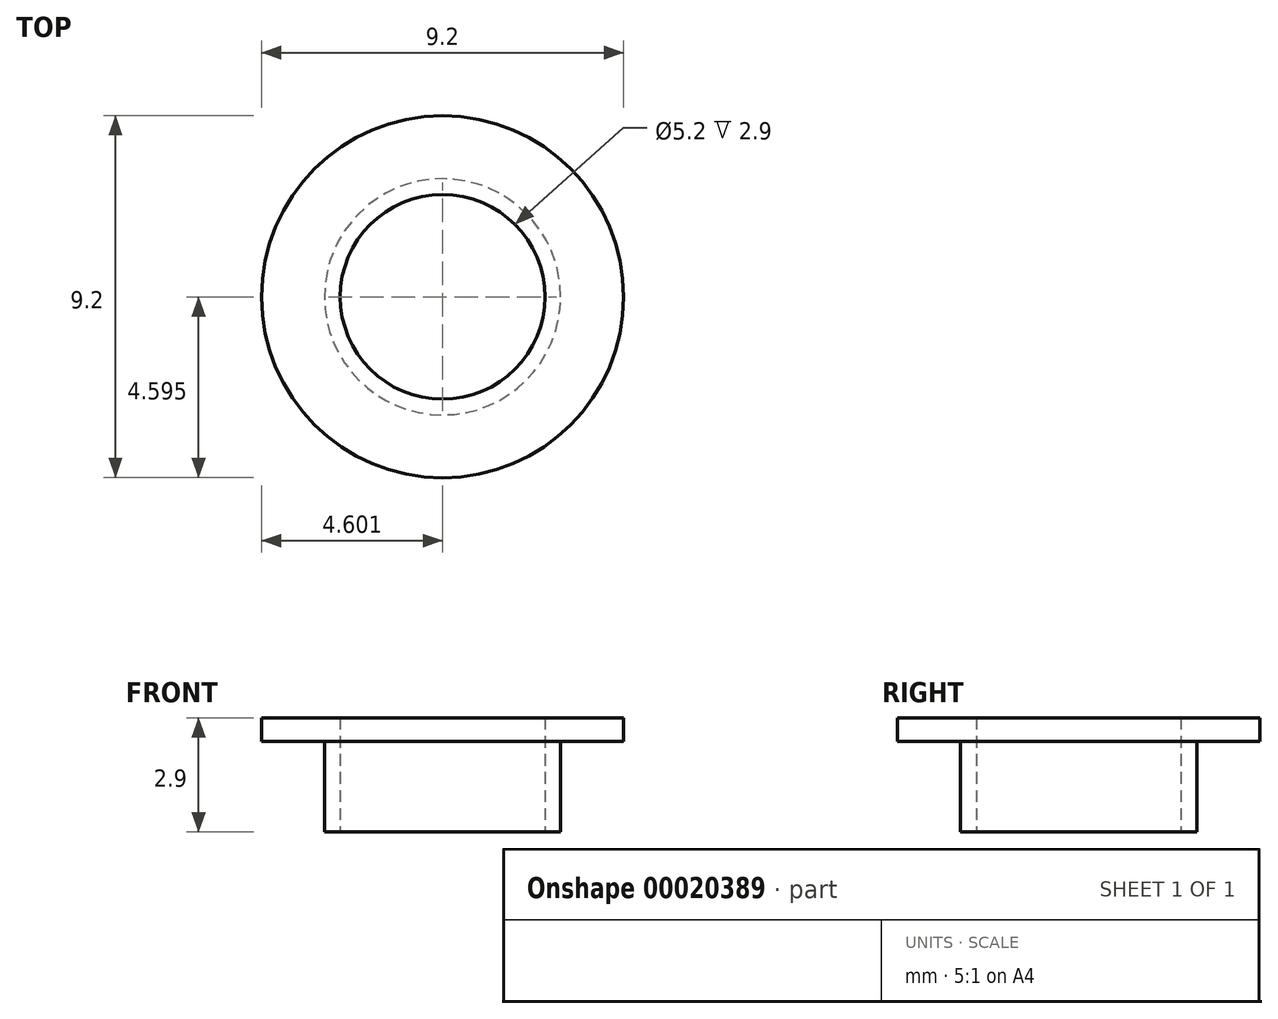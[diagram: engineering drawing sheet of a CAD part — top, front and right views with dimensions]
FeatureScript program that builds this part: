
annotation { "Feature Type Name" : "Feature", "Feature Type Description" : "" }
export const myFeature = defineFeature(function(context is Context, id is Id, definition is map)
    precondition{}
    {
        {
            var Q0;
            Q0=qCreatedBy(makeId("Top.planeOp"),FACE);
            var sketch = newSketch(context, id + "F0", { "sketchPlane" : qUnion([Q0])});
            skLineSegment(sketch, "E0", {"start": v(2.41, 7.8) * mm, "end": v(5.3, 7.8) * mm});
            skLineSegment(sketch, "E1", {"start": v(7.8, 5.3) * mm, "end": v(7.8, 2.41) * mm});
            skLineSegment(sketch, "E2", {"start": v(6.1, 1.7) * mm, "end": v(1.7, 6.1) * mm});
            skPoint(sketch, "E3.visualSharp", {"position": v(7.8, 7.8) * mm});
            skArc(sketch, "E3.filletArc", {"start": v(7.8, 5.3) * mm, "mid": v(7.07, 7.07) * mm, "end": v(5.3, 7.8) * mm});
            skPoint(sketch, "E4.visualSharp", {"position": v(7.8, 0) * mm});
            skArc(sketch, "E4.filletArc", {"start": v(6.1, 1.7) * mm, "mid": v(7.18, 1.5) * mm, "end": v(7.8, 2.41) * mm});
            skPoint(sketch, "E5.visualSharp", {"position": v(0, 7.8) * mm});
            skArc(sketch, "E5.filletArc", {"start": v(2.41, 7.8) * mm, "mid": v(1.5, 7.18) * mm, "end": v(1.7, 6.1) * mm});
            skArc(sketch, "E6.0", {"start": v(7.4, 5.3) * mm, "mid": v(6.78, 6.78) * mm, "end": v(5.3, 7.4) * mm});
            skLineSegment(sketch, "E6.1", {"start": v(7.4, 5.3) * mm, "end": v(7.4, 2.41) * mm});
            skArc(sketch, "E6.2", {"start": v(6.38, 1.99) * mm, "mid": v(7.03, 1.86) * mm, "end": v(7.4, 2.41) * mm});
            skLineSegment(sketch, "E6.3", {"start": v(6.38, 1.99) * mm, "end": v(1.99, 6.38) * mm});
            skArc(sketch, "E6.4", {"start": v(2.41, 7.4) * mm, "mid": v(1.86, 7.03) * mm, "end": v(1.99, 6.38) * mm});
            skLineSegment(sketch, "E6.5", {"start": v(2.41, 7.4) * mm, "end": v(5.3, 7.4) * mm});
            skSolve(sketch);
        }
        {
            var Q0;
            Q0 = qSketchRegion(id + "F0", true);
            extrude(context, id + "F1", {"entities" : qUnion([Q0]), "depth" : 3.5 * mm});
        }
        {
            var Q0;
            Q0=makeQuery(id+"F1.opExtrude","SWEPT_BODY",BODY,{"disambiguationData":[OSD([sQuery(id+"F0.wireOp",EDGE,"E0"),sQuery(id+"F0.wireOp",EDGE,"E1"),sQuery(id+"F0.wireOp",EDGE,"E2"),sQuery(id+"F0.wireOp",EDGE,"E3.filletArc"),sQuery(id+"F0.wireOp",EDGE,"E4.filletArc"),sQuery(id+"F0.wireOp",EDGE,"E5.filletArc"),sQuery(id+"F0.wireOp",EDGE,"E6.0"),sQuery(id+"F0.wireOp",EDGE,"E6.1"),sQuery(id+"F0.wireOp",EDGE,"E6.2"),sQuery(id+"F0.wireOp",EDGE,"E6.3"),sQuery(id+"F0.wireOp",EDGE,"E6.4"),sQuery(id+"F0.wireOp",EDGE,"E6.5")])]});
            deleteBodies(context, id + "F2", {"entities" : qUnion([Q0])});
        }
        {
            var Q0;
            Q0=qCreatedBy(makeId("Top.planeOp"),FACE);
            var sketch = newSketch(context, id + "F3", { "sketchPlane" : qUnion([Q0])});
            skCircle(sketch, "E7", {"center": v(24.56, 9.83) * mm, "radius": 3 * mm});
            skCircle(sketch, "E8", {"center": v(24.56, 9.83) * mm, "radius": 2.6 * mm});
            skSolve(sketch);
        }
        {
            var Q0;
            Q0 = qSketchRegion(id + "F3", true);
            extrude(context, id + "F4", {"entities" : qUnion([Q0]), "depth" : 2.3 * mm});
        }
        {
            var Q0;
            Q0=makeQuery(id+"F4.opExtrude","CAP_FACE",FACE,{"disambiguationData":[OSD([sQuery(id+"F3.wireOp",EDGE,"E7"),sQuery(id+"F3.wireOp",EDGE,"E8")])],"isStart":false});
            var sketch = newSketch(context, id + "F5", { "sketchPlane" : qUnion([Q0])});
            skCircle(sketch, "E9", {"center": v(24.56, 9.83) * mm, "radius": 4.6 * mm});
            skCircle(sketch, "E10", {"center": v(24.56, 9.83) * mm, "radius": 2.6 * mm});
            skSolve(sketch);
        }
        {
            var Q0;
            Q0 = qSketchRegion(id + "F5", true);
            extrude(context, id + "F6", {"entities" : qUnion([Q0]), "operationType" : NewBodyOperationType.ADD, "depth" : 0.6 * mm});
        }
    });
